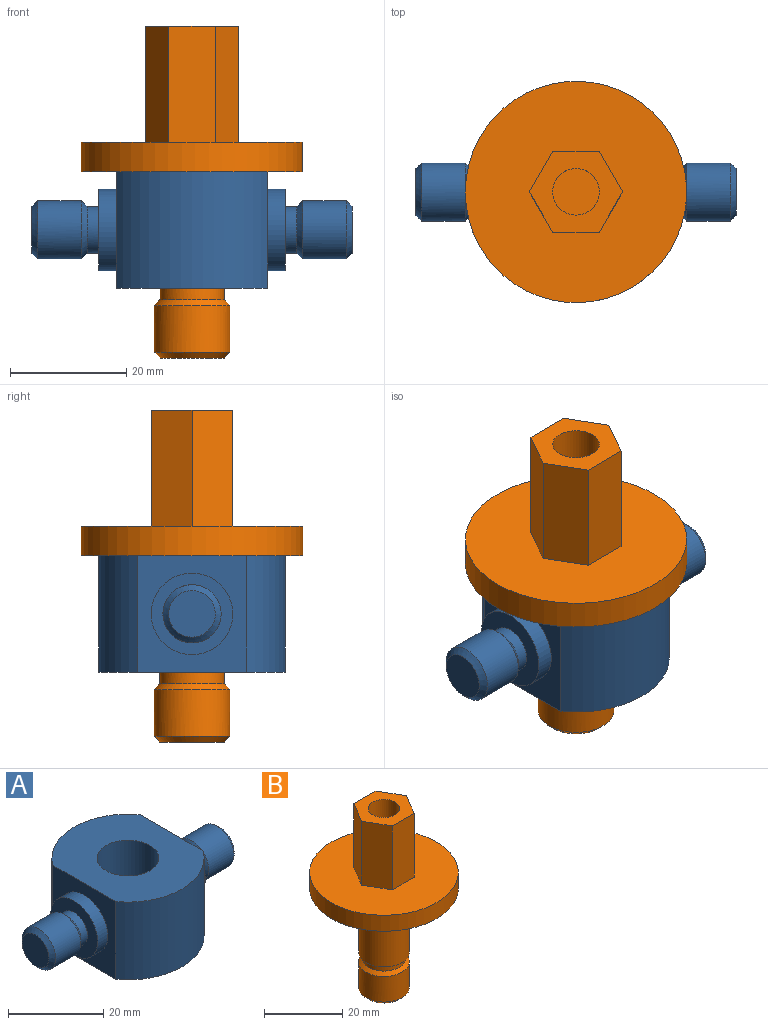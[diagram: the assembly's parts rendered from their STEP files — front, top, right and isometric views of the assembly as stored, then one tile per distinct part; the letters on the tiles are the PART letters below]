
ASSEMBLY  parts=2 mates=1
PART A: 21 faces, bbox 55x32x20 mm
  f0: plane 8x8mm, normal (1,0,0), area 50.3mm2, adj f1
  f1: cone r=0mm half-angle=45deg, axis (-1,0,0), area 40mm2, adj f0,f2
  f2: cylinder r=5mm len=10mm, axis (-1,0,0), area 235.6mm2, adj f1,f4
  f3: plane 8x8mm, normal (-1,0,0), area 50.3mm2, adj f5
  f4: cone r=0mm half-angle=45deg, axis (1,0,0), area 40mm2, adj f2,f6
  f5: cone r=0mm half-angle=45deg, axis (1,0,0), area 40mm2, adj f3,f7
  f6: cylinder r=4mm len=8mm, axis (-1,0,0), area 50.3mm2, adj f4,f8
  f7: cylinder r=5mm len=10mm, axis (1,0,0), area 235.6mm2, adj f5,f9
  f8: plane 14x14mm, normal (1,0,0), area 103.7mm2, adj f6,f10
  f9: cone r=0mm half-angle=45deg, axis (-1,0,0), area 40mm2, adj f7,f11
  f10: cylinder r=7mm len=14mm, axis (-1,0,0), area 131.9mm2, adj f8,f13
  f11: cylinder r=4mm len=8mm, axis (1,0,0), area 50.3mm2, adj f9,f14
  f12: cylinder r=6.5mm len=20mm, axis (0,0,-1), area 816.8mm2, adj f15,f17
  f13: plane 20x18.65mm, normal (1,0,0), area 219.2mm2, adj f10,f15,f16,f17,f18
  f14: plane 14x14mm, normal (-1,0,0), area 103.7mm2, adj f11,f19
  f15: plane 32x26mm, normal (0,0,-1), area 595.4mm2, adj f12,f13,f16,f18,f20
  f16: cylinder r=16mm len=26mm, axis (0,0,-1), area 607mm2, adj f13,f15,f17,f20
  f17: plane 32x26mm, normal (0,0,1), area 595.4mm2, adj f12,f13,f16,f18,f20
  f18: cylinder r=16mm len=26mm, axis (0,0,-1), area 607mm2, adj f13,f15,f17,f20
  f19: cylinder r=7mm len=14mm, axis (1,0,0), area 131.9mm2, adj f14,f20
  f20: plane 20x18.65mm, normal (-1,0,0), area 219.2mm2, adj f15,f16,f17,f18,f19
PART B: 19 faces, bbox 38x38x57 mm
  f0: plane 8x8mm, normal (0,0,1), area 50.3mm2, adj f1
  f1: cylinder r=4mm len=15mm, axis (0,0,-1), area 377mm2, adj f0,f2
  f2: plane 16x13.86mm, normal (0,0,1), area 116mm2, adj f1,f3,f4,f5,f6,f7,f8
  f3: plane 20x6.93mm, normal (0.87,0.5,0), area 160mm2, adj f2,f4,f8,f9
  f4: plane 20x6.93mm, normal (0.87,-0.5,0), area 160mm2, adj f2,f3,f5,f9
  f5: plane 20x8mm, normal (0,-1,0), area 160mm2, adj f2,f4,f6,f9
  f6: plane 20x6.93mm, normal (-0.87,-0.5,0), area 160mm2, adj f2,f5,f7,f9
  f7: plane 20x6.93mm, normal (-0.87,0.5,0), area 160mm2, adj f2,f6,f8,f9
  f8: plane 20x8mm, normal (0,1,0), area 160mm2, adj f2,f3,f7,f9
  f9: plane 38x38mm, normal (0,0,1), area 967.8mm2, adj f3,f4,f5,f6,f7,f8,f10
  f10: cylinder r=19mm len=38mm, axis (0,0,-1), area 596.9mm2, adj f9,f11
  f11: plane 38x38mm, normal (0,0,-1), area 1001.4mm2, adj f10,f12
  f12: cylinder r=6.5mm len=20mm, axis (0,0,1), area 816.8mm2, adj f11,f13
  f13: plane 13x13mm, normal (0,0,-1), area 37.7mm2, adj f12,f15
  f14: plane 11x11mm, normal (0,0,-1), area 95mm2, adj f16
  f15: cylinder r=5.5mm len=11mm, axis (0,0,1), area 69.1mm2, adj f13,f17
  f16: cone r=0mm half-angle=45deg, axis (0,0,1), area 53.3mm2, adj f14,f18
  f17: cone r=0mm half-angle=45deg, axis (0,0,-1), area 53.3mm2, adj f15,f18
  f18: cylinder r=6.5mm len=13mm, axis (0,0,1), area 326.7mm2, adj f16,f17
PLACE A rot(axis=(0,0,1),180deg) t=(-37.01,30.01,-63.26)mm
PLACE B t=(-37.01,30.01,-63.26)mm
MATE revolute A.f12 <-> B.f1  axis (0,0,1) through (-37.01,30.01,-53.26)mm
